# Revit family: Electrical_Equipment-Floor_Box-Hubbell_Wiring-8_Gang-Ball_Room-CFB8FC1
name_source: partatom
category: Electrical Fixtures
revit_build: Autodesk Revit 2015 (Build: 20140606_1530(x64)
units: mm (PartAtom-declared; Revit-internal decimal feet)

## types (1)
- CFB8FC1
    Assembly Code = D5020115
    Box Material = Metal - Hubbell - Steel
    Conduit Connector 1 Radius = 0.75 "
    Conduit Connector_1 Description = Conduit 1.5in. 1.25in. or 1in. Connection
    Conduit Connector_10 Description = Conduit 1.5in. 1.25in. or 1in. Connection
    Conduit Connector_11 Description = Conduit 1.5in. 1.25in. or 1in. Connection
    Conduit Connector_12 Description = Conduit 1.5in. 1.25in. or 1in. Connection
    Conduit Connector_2 Description = Conduit 1.5in. 1.25in. or 1in. Connection
    Conduit Connector_3 Description = Conduit 1.5in. 1.25in. or 1in. Connection
    Conduit Connector_4 Description = Conduit 1.5in. 1.25in. or 1in. Connection
    Conduit Connector_5 Description = Conduit 1.5in. 1.25in. or 1in. Connection
    Conduit Connector_6 Description = Conduit 1.5in. 1.25in. or 1in. Connection
    Conduit Connector_7 Description = Conduit 1.5in. 1.25in. or 1in. Connection
    Conduit Connector_8 Description = Conduit 1.5in. 1.25in. or 1in. Connection
    Conduit Connector_9 Description = Conduit 1.5in. 1.25in. or 1in. Connection
    Default Elevation = 0 "
    Description = Recessed Ballroom Series Floor Boxes 8 Gang, Carpet
    Manufacturer = Hubbell-Wiring
    Model = CFB8FC1
    Product Documentation Link = http://www.hubbell-wiring.com
    Product Page URL = http://ecatalog.hubbell-wiring.com
    Product data url = https://bimobject.com
    URL = http://www.hubbell-wiring.com

## geometry (parser evidence)
native form markers: Blend x5, Sweep x3
no freeform markers — native parametric forms only
